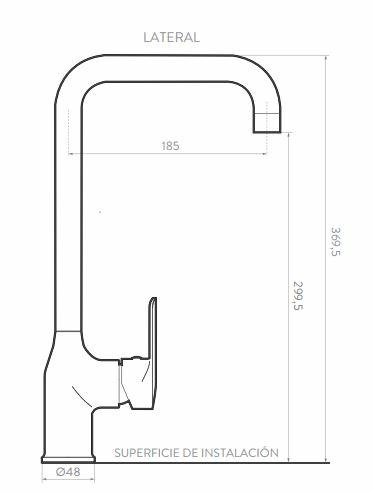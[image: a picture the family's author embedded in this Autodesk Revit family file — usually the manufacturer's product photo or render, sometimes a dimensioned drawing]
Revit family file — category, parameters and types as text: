
# Revit family: KR5010001_Grifería para Lavaplatos Monocontrol Koral
name_source: partatom
category: Plumbing Fixtures
units: mm (PartAtom-declared; Revit-internal decimal feet)

## family parameters
Cut with Voids When Loaded = No
Host = Face
Part Type = Normal
Room Calculation Point = No
Round Connector Dimension = Use Diameter
Shared = No

## types (1)
- KR5010001_Grifería para Lavaplatos Monocontrol Koral
    Alto = 370 mm
    Ancho = 48 mm  [stored 0.15748 ft]
    Capacidad de flujo = 60 psi: 7,28 L/min
    Creado por = IDD
    Default Elevation = 1219 mm
    Dimensiones generales producto (H * W * D) = 988 gr. - 2,17 lb
    Fabricante = Corona
    Fecha de creación = 05/08/2020
    Garantía = 30 años
    Material = Corona_Acero
    Peso Neto aprox = 988 gr. - 2,17 lb
    Presion maxima = 125 psi (862 Kpa)
    Presion minima = 20 psi (138 Kpa)
    Profundidad = 221 mm
    Temperatura de uso = 4ºC a 60ºC
    URL = https://corona.co

note: [stored X ft] marks values corroborated as IEEE doubles in the binary element streams (Revit-internal decimal feet)

## geometry (parser evidence)
native form markers: Sweep x3
no freeform markers — native parametric forms only
